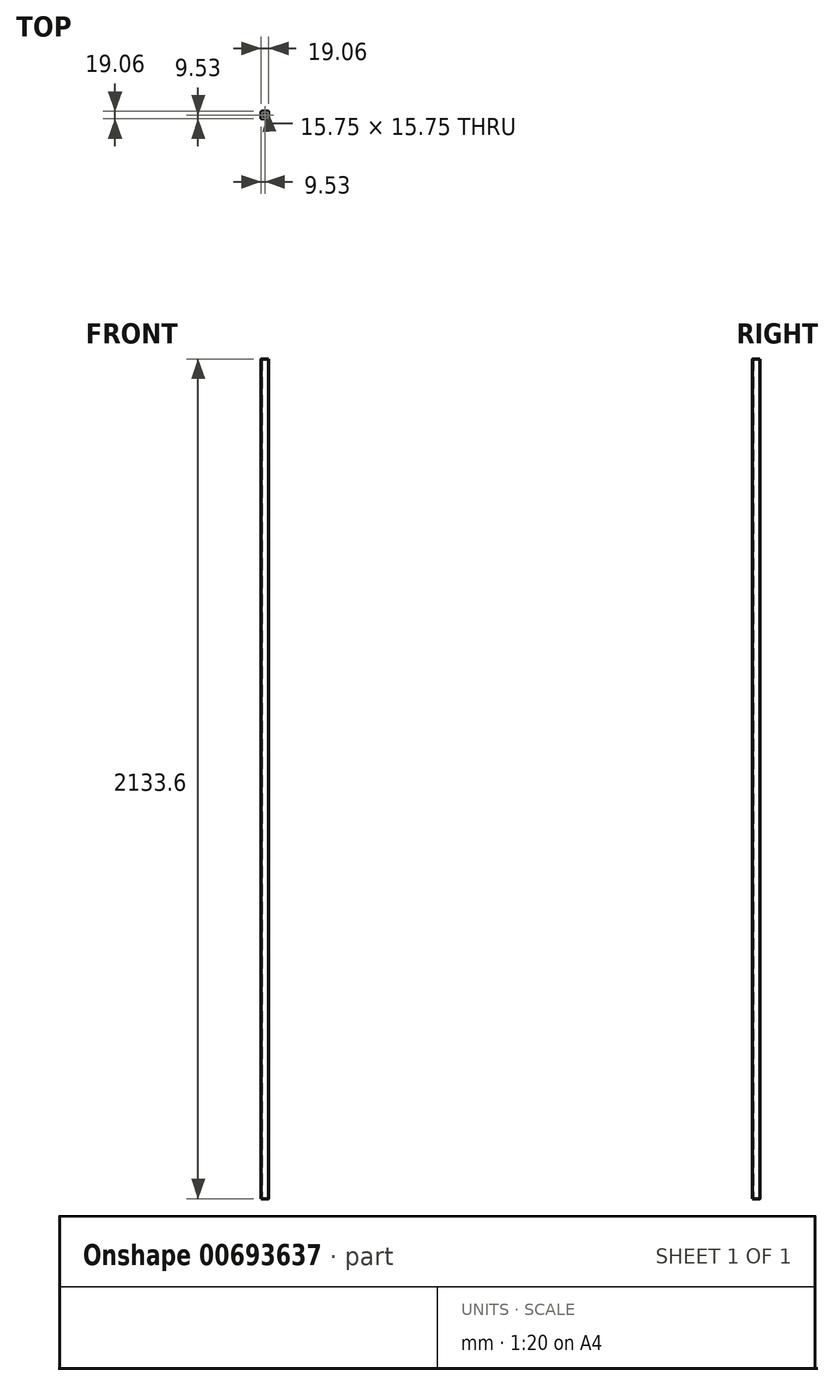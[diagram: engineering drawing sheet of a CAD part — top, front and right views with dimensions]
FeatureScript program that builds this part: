
annotation { "Feature Type Name" : "Feature", "Feature Type Description" : "" }
export const myFeature = defineFeature(function(context is Context, id is Id, definition is map)
    precondition{}
    {
        {
            var Q0;
            Q0=qCreatedBy(makeId("Top.planeOp"),FACE);
            var sketch = newSketch(context, id + "F0", { "sketchPlane" : qUnion([Q0])});
            skLineSegment(sketch, "E0.bottom", {"start": v(-8.02, 9.52) * mm, "end": v(8.03, 9.52) * mm});
            skLineSegment(sketch, "E0.top", {"start": v(-8.03, -9.53) * mm, "end": v(8.03, -9.53) * mm});
            skLineSegment(sketch, "E0.left", {"start": v(-9.52, 8.02) * mm, "end": v(-9.53, -8.03) * mm});
            skLineSegment(sketch, "E0.right", {"start": v(9.53, 8.02) * mm, "end": v(9.53, -8.03) * mm});
            skPoint(sketch, "E0.middle", {"position": v(0, 0) * mm});
            skPoint(sketch, "E1.visualSharp", {"position": v(-9.52, 9.52) * mm});
            skArc(sketch, "E1.filletArc", {"start": v(-8.02, 9.52) * mm, "mid": v(-9.09, 9.09) * mm, "end": v(-9.52, 8.02) * mm});
            skPoint(sketch, "E2.visualSharp", {"position": v(9.53, 9.52) * mm});
            skArc(sketch, "E2.filletArc", {"start": v(9.53, 8.02) * mm, "mid": v(9.09, 9.09) * mm, "end": v(8.03, 9.52) * mm});
            skPoint(sketch, "E3.visualSharp", {"position": v(9.53, -9.53) * mm});
            skArc(sketch, "E3.filletArc", {"start": v(8.03, -9.53) * mm, "mid": v(9.09, -9.09) * mm, "end": v(9.53, -8.03) * mm});
            skPoint(sketch, "E4.visualSharp", {"position": v(-9.53, -9.53) * mm});
            skArc(sketch, "E4.filletArc", {"start": v(-9.53, -8.03) * mm, "mid": v(-9.09, -9.09) * mm, "end": v(-8.03, -9.53) * mm});
            skLineSegment(sketch, "E5.0", {"start": v(-7.87, 7.87) * mm, "end": v(7.87, 7.87) * mm});
            skLineSegment(sketch, "E5.1", {"start": v(-7.87, 7.87) * mm, "end": v(-7.87, -7.87) * mm});
            skLineSegment(sketch, "E5.2", {"start": v(-7.87, -7.87) * mm, "end": v(7.87, -7.87) * mm});
            skLineSegment(sketch, "E5.3", {"start": v(7.87, 7.87) * mm, "end": v(7.87, -7.87) * mm});
            skSolve(sketch);
        }
        {
            var Q0;
            Q0=makeQuery(id+"F0.imprint","IMPRINT",FACE,{"disambiguationData":[TD([[makeQuery(id+"F0.imprint","IMPRINT",EDGE,{"derivedFrom":sQuery(id+"F0.wireOp",EDGE,"E0.bottom")}),-1.0]])]});
            extrude(context, id + "F1", {"entities" : qUnion([Q0]), "depth" : 13.5 * 152.4 * mm + 76.2 * mm});
        }
    });
